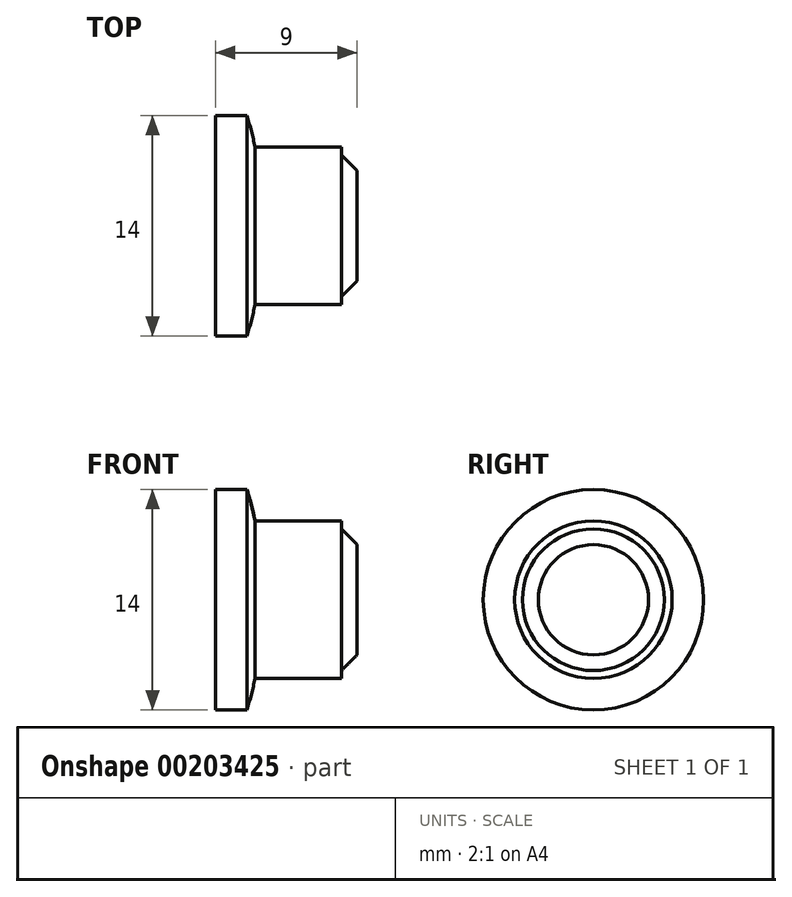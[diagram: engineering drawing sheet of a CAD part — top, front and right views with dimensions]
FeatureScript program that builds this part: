
annotation { "Feature Type Name" : "Feature", "Feature Type Description" : "" }
export const myFeature = defineFeature(function(context is Context, id is Id, definition is map)
    precondition{}
    {
        {
            var Q0;
            Q0=qCreatedBy(makeId("Front.planeOp"),FACE);
            var sketch = newSketch(context, id + "F0", { "sketchPlane" : qUnion([Q0])});
            skArc(sketch, "E0", {"start": v(0, 0) * mm, "mid": v(-0.26, 3.54) * mm, "end": v(-1.04, 7) * mm});
            skLineSegment(sketch, "E1", {"start": v(-1.04, 7) * mm, "end": v(-3.04, 7) * mm});
            skLineSegment(sketch, "E2", {"start": v(-3.04, 7) * mm, "end": v(-3.04, 0) * mm});
            skLineSegment(sketch, "E3", {"start": v(-3.04, 0) * mm, "end": v(0, 0) * mm});
            skSolve(sketch);
        }
        {
            var Q0;
            Q0 = qSketchRegion(id + "F0", true);
            var Q1;
            Q1=sQuery(id+"F0.wireOp",EDGE,"E3");
            revolve(context, id + "F1", {"entities" : qUnion([Q0]), "axis" : qUnion([Q1]), "revolveType" : RevolveType.FULL});
        }
        {
            var Q0;
            Q0=makeQuery(id+"F1.opRevolve","SWEPT_FACE",FACE,{"disambiguationData":[OSD([sQuery(id+"F0.wireOp",EDGE,"E2")])]});
            var sketch = newSketch(context, id + "F2", { "sketchPlane" : qUnion([Q0])});
            skCircle(sketch, "E4", {"center": v(0, 0) * mm, "radius": 5 * mm});
            skSolve(sketch);
        }
        {
            var Q0;
            Q0 = qSketchRegion(id + "F2", true);
            extrude(context, id + "F3", {"entities" : qUnion([Q0]), "operationType" : NewBodyOperationType.ADD, "oppositeDirection" : true, "depth" : 8 * mm});
        }
        {
            var Q0;
            Q0=makeQuery(id+"F3.opExtrude","CAP_FACE",FACE,{"disambiguationData":[OSD([sQuery(id+"F2.wireOp",EDGE,"E4")])],"isStart":false});
            var sketch = newSketch(context, id + "F4", { "sketchPlane" : qUnion([Q0])});
            skCircle(sketch, "E5.0", {"center": v(0, 0) * mm, "radius": 4.5 * mm});
            skSolve(sketch);
        }
        {
            var Q0;
            Q0 = qSketchRegion(id + "F4", true);
            extrude(context, id + "F5", {"entities" : qUnion([Q0]), "operationType" : NewBodyOperationType.ADD, "depth" : 1 * mm});
        }
        {
            var Q0;
            Q0=makeQuery(id+"F5.opExtrude","CAP_EDGE",EDGE,{"disambiguationData":[OSD([sQuery(id+"F4.wireOp",EDGE,"E5.0")])],"isStart":false});
            chamfer(context, id + "F6", {"entities" : qUnion([Q0]), "width" : 1 * mm, "tangentPropagation" : true});
        }
    });
